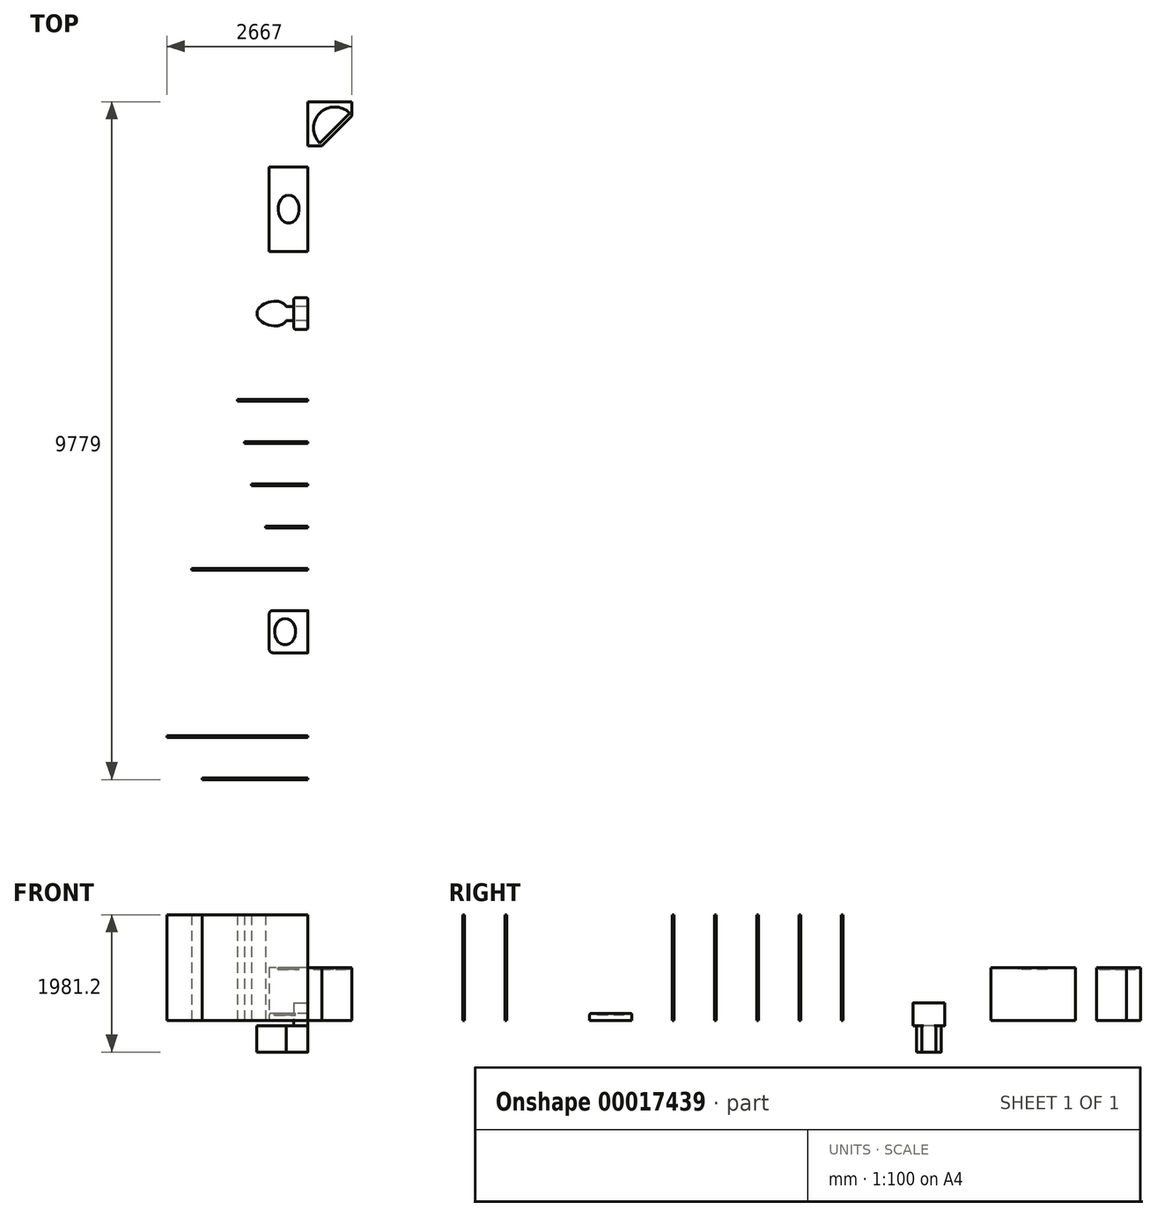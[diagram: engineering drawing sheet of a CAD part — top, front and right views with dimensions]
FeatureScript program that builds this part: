
annotation { "Feature Type Name" : "Feature", "Feature Type Description" : "" }
export const myFeature = defineFeature(function(context is Context, id is Id, definition is map)
    precondition{}
    {
        {
            var Q0;
            Q0=qCreatedBy(makeId("Top.planeOp"),FACE);
            cPlane(context, id + "F0", {"entities" : qUnion([Q0]), "cplaneType" : CPlaneType.OFFSET, "offset" : 457.2 * mm, "width" : 152.4 * mm, "height" : 152.4 * mm});
        }
        {
            var Q0;
            Q0=qCreatedBy(makeId("Top.planeOp"),FACE);
            var sketch = newSketch(context, id + "F1", { "sketchPlane" : qUnion([Q0])});
            skLineSegment(sketch, "E0", {"start": v(0, 702.51) * mm, "end": v(0, 550.11) * mm});
            skLineSegment(sketch, "E1", {"start": v(-25.4, 727.91) * mm, "end": v(-311.29, 727.91) * mm});
            skLineSegment(sketch, "E2", {"start": v(-25.4, 524.71) * mm, "end": v(-311.29, 524.71) * mm});
            skLineSegment(sketch, "E3", {"start": v(-457.2, 626.31) * mm, "end": v(-736.6, 626.31) * mm, "construction": true});
            skLineSegment(sketch, "E4", {"start": v(-457.2, 804.11) * mm, "end": v(-457.2, 448.51) * mm, "construction": true});
            skEllipticalArc(sketch, "E5", {});
            skArc(sketch, "E6", {"start": v(-457.2, 448.51) * mm, "mid": v(-374.9, 468.7) * mm, "end": v(-311.29, 524.71) * mm});
            skArc(sketch, "E7", {"start": v(-311.29, 727.91) * mm, "mid": v(-374.9, 783.92) * mm, "end": v(-457.2, 804.11) * mm});
            skArc(sketch, "E8", {"start": v(-311.29, 524.71) * mm, "mid": v(-279.4, 626.31) * mm, "end": v(-311.29, 727.91) * mm, "construction": true});
            skLineSegment(sketch, "E9", {"start": v(-736.6, 626.31) * mm, "end": v(0, 626.31) * mm, "construction": true});
            skPoint(sketch, "E10.visualSharp", {"position": v(0, 727.91) * mm});
            skArc(sketch, "E10.filletArc", {"start": v(0, 702.51) * mm, "mid": v(-7.44, 720.47) * mm, "end": v(-25.4, 727.91) * mm});
            skPoint(sketch, "E11.visualSharp", {"position": v(0, 524.71) * mm});
            skArc(sketch, "E11.filletArc", {"start": v(-25.4, 524.71) * mm, "mid": v(-7.44, 532.15) * mm, "end": v(0, 550.11) * mm});
            const initialGuessF1  = {"E5": [-0.4572, 0.6263124527790692, 0, 1, 0.1778, 0.2794, 6.283185307179586, 3.141592653589793]};
            skSetInitialGuess(sketch, initialGuessF1);
            skSolve(sketch);
        }
        {
            var Q0;
            Q0 = qSketchRegion(id + "F1", true);
            extrude(context, id + "F2", {"entities" : qUnion([Q0]), "depth" : 381 * mm});
        }
        {
            var Q0;
            Q0=makeQuery(id+"F2.opExtrude","CAP_FACE",FACE,{"disambiguationData":[OSD([sQuery(id+"F1.wireOp",EDGE,"E0"),sQuery(id+"F1.wireOp",EDGE,"E1"),sQuery(id+"F1.wireOp",EDGE,"E2"),sQuery(id+"F1.wireOp",EDGE,"E5"),sQuery(id+"F1.wireOp",EDGE,"E6"),sQuery(id+"F1.wireOp",EDGE,"E7"),sQuery(id+"F1.wireOp",EDGE,"E10.filletArc"),sQuery(id+"F1.wireOp",EDGE,"E11.filletArc")])],"isStart":false});
            var sketch = newSketch(context, id + "F3", { "sketchPlane" : qUnion([Q0])});
            skLineSegment(sketch, "E12.bottom", {"start": v(-177.8, 854.91) * mm, "end": v(-25.4, 854.91) * mm});
            skLineSegment(sketch, "E12.top", {"start": v(-177.8, 397.71) * mm, "end": v(-25.4, 397.71) * mm});
            skLineSegment(sketch, "E12.left", {"start": v(-203.2, 829.51) * mm, "end": v(-203.2, 423.11) * mm});
            skLineSegment(sketch, "E12.right", {"start": v(0, 829.51) * mm, "end": v(0, 423.11) * mm});
            skPoint(sketch, "E13.visualSharp", {"position": v(-203.2, 854.91) * mm});
            skArc(sketch, "E13.filletArc", {"start": v(-177.8, 854.91) * mm, "mid": v(-195.76, 847.47) * mm, "end": v(-203.2, 829.51) * mm});
            skPoint(sketch, "E14.visualSharp", {"position": v(0, 854.91) * mm});
            skArc(sketch, "E14.filletArc", {"start": v(0, 829.51) * mm, "mid": v(-7.44, 847.47) * mm, "end": v(-25.4, 854.91) * mm});
            skPoint(sketch, "E15.visualSharp", {"position": v(0, 397.71) * mm});
            skArc(sketch, "E15.filletArc", {"start": v(-25.4, 397.71) * mm, "mid": v(-7.44, 405.15) * mm, "end": v(0, 423.11) * mm});
            skPoint(sketch, "E16.visualSharp", {"position": v(-203.2, 397.71) * mm});
            skArc(sketch, "E16.filletArc", {"start": v(-203.2, 423.11) * mm, "mid": v(-195.76, 405.15) * mm, "end": v(-177.8, 397.71) * mm});
            skSolve(sketch);
        }
        {
            var Q0;
            Q0 = qSketchRegion(id + "F3", true);
            extrude(context, id + "F4", {"entities" : qUnion([Q0]), "operationType" : NewBodyOperationType.ADD, "depth" : 330.2 * mm});
        }
        {
            var Q0;
            Q0=qCreatedBy(id+"F0.planeOp",FACE);
            var sketch = newSketch(context, id + "F5", { "sketchPlane" : qUnion([Q0])});
            skLineSegment(sketch, "E17.bottom", {"start": v(0, 1524) * mm, "end": v(-558.8, 1524) * mm});
            skLineSegment(sketch, "E17.top", {"start": v(0, 2743.2) * mm, "end": v(-558.8, 2743.2) * mm});
            skLineSegment(sketch, "E17.left", {"start": v(0, 1524) * mm, "end": v(0, 2743.2) * mm});
            skLineSegment(sketch, "E17.right", {"start": v(-558.8, 1524) * mm, "end": v(-558.8, 2743.2) * mm});
            skSolve(sketch);
        }
        {
            var Q0;
            Q0 = qSketchRegion(id + "F5", true);
            extrude(context, id + "F6", {"entities" : qUnion([Q0]), "depth" : 762 * mm});
        }
        {
            var Q0;
            Q0=makeQuery(id+"F6.opExtrude","CAP_FACE",FACE,{"disambiguationData":[OSD([sQuery(id+"F5.wireOp",EDGE,"E17.bottom"),sQuery(id+"F5.wireOp",EDGE,"E17.top"),sQuery(id+"F5.wireOp",EDGE,"E17.left"),sQuery(id+"F5.wireOp",EDGE,"E17.right")])],"isStart":false});
            var sketch = newSketch(context, id + "F7", { "sketchPlane" : qUnion([Q0])});
            skLineSegment(sketch, "E18", {"start": v(0, 2133.6) * mm, "end": v(-558.8, 2133.6) * mm, "construction": true});
            skLineSegment(sketch, "E19", {"start": v(-279.4, 2743.2) * mm, "end": v(-279.4, 1524) * mm, "construction": true});
            skEllipse(sketch, "E20", {"center": v(-279.4, 2133.6) * mm, "majorRadius": 203.15 * mm, "minorRadius": 152.4 * mm, "majorAxis": v(0, 1)});
            skSolve(sketch);
        }
        {
            var Q0;
            Q0 = qSketchRegion(id + "F7", true);
            extrude(context, id + "F8", {"entities" : qUnion([Q0]), "operationType" : NewBodyOperationType.REMOVE, "oppositeDirection" : true, "depth" : 30.48 * mm});
        }
        {
            var Q0;
            Q0=qCreatedBy(id+"F0.planeOp",FACE);
            var sketch = newSketch(context, id + "F9", { "sketchPlane" : qUnion([Q0])});
            skLineSegment(sketch, "E21", {"start": v(0, 3048) * mm, "end": v(203.2, 3048) * mm});
            skLineSegment(sketch, "E22", {"start": v(203.2, 3048) * mm, "end": v(635, 3479.8) * mm});
            skLineSegment(sketch, "E23", {"start": v(635, 3479.8) * mm, "end": v(635, 3683) * mm});
            skLineSegment(sketch, "E24", {"start": v(635, 3683) * mm, "end": v(0, 3683) * mm});
            skLineSegment(sketch, "E25", {"start": v(0, 3683) * mm, "end": v(0, 3048) * mm});
            skSolve(sketch);
        }
        {
            var Q0;
            Q0 = qSketchRegion(id + "F9", true);
            extrude(context, id + "F10", {"entities" : qUnion([Q0]), "depth" : 762 * mm});
        }
        {
            var Q0;
            Q0=makeQuery(id+"F10.opExtrude","CAP_FACE",FACE,{"disambiguationData":[OSD([sQuery(id+"F9.wireOp",EDGE,"E21"),sQuery(id+"F9.wireOp",EDGE,"E22"),sQuery(id+"F9.wireOp",EDGE,"E23"),sQuery(id+"F9.wireOp",EDGE,"E24"),sQuery(id+"F9.wireOp",EDGE,"E25")])],"isStart":false});
            var sketch = newSketch(context, id + "F11", { "sketchPlane" : qUnion([Q0])});
            skLineSegment(sketch, "E26", {"start": v(0, 3683) * mm, "end": v(419.1, 3263.9) * mm, "construction": true});
            skLineSegment(sketch, "E27.0", {"start": v(169.6, 3086.25) * mm, "end": v(600.66, 3517.3) * mm});
            skArc(sketch, "E28", {"start": v(600.66, 3517.3) * mm, "mid": v(169.6, 3517.3) * mm, "end": v(169.6, 3086.25) * mm});
            skSolve(sketch);
        }
        {
            var Q0;
            Q0 = qSketchRegion(id + "F11", true);
            extrude(context, id + "F12", {"entities" : qUnion([Q0]), "operationType" : NewBodyOperationType.REMOVE, "oppositeDirection" : true, "depth" : 30.48 * mm});
        }
        {
            var Q0;
            Q0=qCreatedBy(id+"F0.planeOp",FACE);
            var sketch = newSketch(context, id + "F13", { "sketchPlane" : qUnion([Q0])});
            skLineSegment(sketch, "E29.bottom", {"start": v(0, -5486.4) * mm, "end": v(-2032, -5486.4) * mm});
            skLineSegment(sketch, "E29.top", {"start": v(0, -5461) * mm, "end": v(-2032, -5461) * mm});
            skLineSegment(sketch, "E29.left", {"start": v(0, -5461) * mm, "end": v(0, -5486.4) * mm});
            skLineSegment(sketch, "E29.right", {"start": v(-2032, -5461) * mm, "end": v(-2032, -5486.4) * mm});
            skSolve(sketch);
        }
        {
            var Q0;
            Q0 = qSketchRegion(id + "F13", true);
            extrude(context, id + "F14", {"entities" : qUnion([Q0]), "depth" : 1524 * mm});
        }
        {
            var Q0;
            Q0=qCreatedBy(id+"F0.planeOp",FACE);
            var sketch = newSketch(context, id + "F15", { "sketchPlane" : qUnion([Q0])});
            skLineSegment(sketch, "E30.bottom", {"start": v(0, -6096) * mm, "end": v(-1524, -6096) * mm});
            skLineSegment(sketch, "E30.top", {"start": v(0, -6070.6) * mm, "end": v(-1524, -6070.6) * mm});
            skLineSegment(sketch, "E30.left", {"start": v(0, -6070.6) * mm, "end": v(0, -6096) * mm});
            skLineSegment(sketch, "E30.right", {"start": v(-1524, -6070.6) * mm, "end": v(-1524, -6096) * mm});
            skSolve(sketch);
        }
        {
            var Q0;
            Q0 = qSketchRegion(id + "F15", true);
            extrude(context, id + "F16", {"entities" : qUnion([Q0]), "depth" : 1524 * mm});
        }
        {
            var Q0;
            Q0=qCreatedBy(id+"F0.planeOp",FACE);
            var sketch = newSketch(context, id + "F17", { "sketchPlane" : qUnion([Q0])});
            skLineSegment(sketch, "E31.bottom", {"start": v(0, -609.6) * mm, "end": v(-1016, -609.6) * mm});
            skLineSegment(sketch, "E31.top", {"start": v(0, -635) * mm, "end": v(-1016, -635) * mm});
            skLineSegment(sketch, "E31.left", {"start": v(0, -609.6) * mm, "end": v(0, -635) * mm});
            skLineSegment(sketch, "E31.right", {"start": v(-1016, -609.6) * mm, "end": v(-1016, -635) * mm});
            skSolve(sketch);
        }
        {
            var Q0;
            Q0 = qSketchRegion(id + "F17", true);
            extrude(context, id + "F18", {"entities" : qUnion([Q0]), "depth" : 1524 * mm});
        }
        {
            var Q0;
            Q0=qCreatedBy(id+"F0.planeOp",FACE);
            var sketch = newSketch(context, id + "F19", { "sketchPlane" : qUnion([Q0])});
            skLineSegment(sketch, "E32.bottom", {"start": v(0, -1219.2) * mm, "end": v(-914.4, -1219.2) * mm});
            skLineSegment(sketch, "E32.top", {"start": v(0, -1244.6) * mm, "end": v(-914.4, -1244.6) * mm});
            skLineSegment(sketch, "E32.left", {"start": v(0, -1219.2) * mm, "end": v(0, -1244.6) * mm});
            skLineSegment(sketch, "E32.right", {"start": v(-914.4, -1219.2) * mm, "end": v(-914.4, -1244.6) * mm});
            skSolve(sketch);
        }
        {
            var Q0;
            Q0 = qSketchRegion(id + "F19", true);
            extrude(context, id + "F20", {"entities" : qUnion([Q0]), "depth" : 1524 * mm});
        }
        {
            var Q0;
            Q0=qCreatedBy(id+"F0.planeOp",FACE);
            var sketch = newSketch(context, id + "F21", { "sketchPlane" : qUnion([Q0])});
            skLineSegment(sketch, "E33.bottom", {"start": v(0, -1828.8) * mm, "end": v(-812.8, -1828.8) * mm});
            skLineSegment(sketch, "E33.top", {"start": v(0, -1854.2) * mm, "end": v(-812.8, -1854.2) * mm});
            skLineSegment(sketch, "E33.left", {"start": v(0, -1828.8) * mm, "end": v(0, -1854.2) * mm});
            skLineSegment(sketch, "E33.right", {"start": v(-812.8, -1828.8) * mm, "end": v(-812.8, -1854.2) * mm});
            skSolve(sketch);
        }
        {
            var Q0;
            Q0 = qSketchRegion(id + "F21", true);
            extrude(context, id + "F22", {"entities" : qUnion([Q0]), "depth" : 1524 * mm});
        }
        {
            var Q0;
            Q0=qCreatedBy(id+"F0.planeOp",FACE);
            var sketch = newSketch(context, id + "F23", { "sketchPlane" : qUnion([Q0])});
            skLineSegment(sketch, "E34.bottom", {"start": v(0, -2438.4) * mm, "end": v(-609.6, -2438.4) * mm});
            skLineSegment(sketch, "E34.top", {"start": v(0, -2463.8) * mm, "end": v(-609.6, -2463.8) * mm});
            skLineSegment(sketch, "E34.left", {"start": v(0, -2438.4) * mm, "end": v(0, -2463.8) * mm});
            skLineSegment(sketch, "E34.right", {"start": v(-609.6, -2438.4) * mm, "end": v(-609.6, -2463.8) * mm});
            skSolve(sketch);
        }
        {
            var Q0;
            Q0 = qSketchRegion(id + "F23", true);
            extrude(context, id + "F24", {"entities" : qUnion([Q0]), "depth" : 1524 * mm});
        }
        {
            var Q0;
            Q0=qCreatedBy(id+"F0.planeOp",FACE);
            var sketch = newSketch(context, id + "F25", { "sketchPlane" : qUnion([Q0])});
            skLineSegment(sketch, "E35.bottom", {"start": v(0, -3048) * mm, "end": v(-1676.4, -3048) * mm});
            skLineSegment(sketch, "E35.top", {"start": v(0, -3073.39) * mm, "end": v(-1676.4, -3073.39) * mm});
            skLineSegment(sketch, "E35.left", {"start": v(0, -3048) * mm, "end": v(0, -3073.39) * mm});
            skLineSegment(sketch, "E35.right", {"start": v(-1676.4, -3048) * mm, "end": v(-1676.4, -3073.39) * mm});
            skSolve(sketch);
        }
        {
            var Q0;
            Q0 = qSketchRegion(id + "F25", true);
            extrude(context, id + "F26", {"entities" : qUnion([Q0]), "depth" : 1524 * mm});
        }
        {
            var Q0;
            Q0=qCreatedBy(id+"F0.planeOp",FACE);
            var sketch = newSketch(context, id + "F27", { "sketchPlane" : qUnion([Q0])});
            skLineSegment(sketch, "E36.bottom", {"start": v(0, -3657.6) * mm, "end": v(-508, -3657.6) * mm});
            skLineSegment(sketch, "E36.top", {"start": v(0, -4267.2) * mm, "end": v(-508, -4267.2) * mm});
            skLineSegment(sketch, "E36.left", {"start": v(0, -3657.6) * mm, "end": v(0, -4267.2) * mm});
            skLineSegment(sketch, "E36.right", {"start": v(-558.8, -3708.4) * mm, "end": v(-558.8, -4216.4) * mm});
            skPoint(sketch, "E37.visualSharp", {"position": v(-558.8, -3657.6) * mm});
            skArc(sketch, "E37.filletArc", {"start": v(-508, -3657.6) * mm, "mid": v(-543.92, -3672.48) * mm, "end": v(-558.8, -3708.4) * mm});
            skPoint(sketch, "E38.visualSharp", {"position": v(-558.8, -4267.2) * mm});
            skArc(sketch, "E38.filletArc", {"start": v(-558.8, -4216.4) * mm, "mid": v(-543.92, -4252.32) * mm, "end": v(-508, -4267.2) * mm});
            skSolve(sketch);
        }
        {
            var Q0;
            Q0 = qSketchRegion(id + "F27", true);
            extrude(context, id + "F28", {"entities" : qUnion([Q0]), "depth" : 101.6 * mm});
        }
        {
            var Q0;
            Q0=makeQuery(id+"F28.opExtrude","CAP_FACE",FACE,{"disambiguationData":[OSD([sQuery(id+"F27.wireOp",EDGE,"E36.bottom"),sQuery(id+"F27.wireOp",EDGE,"E36.top"),sQuery(id+"F27.wireOp",EDGE,"E36.left"),sQuery(id+"F27.wireOp",EDGE,"E36.right"),sQuery(id+"F27.wireOp",EDGE,"E37.filletArc"),sQuery(id+"F27.wireOp",EDGE,"E38.filletArc")])],"isStart":false});
            var sketch = newSketch(context, id + "F29", { "sketchPlane" : qUnion([Q0])});
            skLineSegment(sketch, "E39", {"start": v(-558.8, -3962.4) * mm, "end": v(0, -3962.4) * mm, "construction": true});
            skEllipse(sketch, "E40", {"center": v(-330.2, -3962.4) * mm, "majorRadius": 190.5 * mm, "minorRadius": 152.4 * mm, "majorAxis": v(0, 1)});
            skSolve(sketch);
        }
        {
            var Q0;
            Q0 = qSketchRegion(id + "F29", true);
            extrude(context, id + "F30", {"entities" : qUnion([Q0]), "operationType" : NewBodyOperationType.REMOVE, "oppositeDirection" : true, "depth" : 30.48 * mm});
        }
        {
            var Q0;
            Q0=makeQuery(id+"F28.opExtrude","CAP_EDGE",EDGE,{"disambiguationData":[OSD([sQuery(id+"F27.wireOp",EDGE,"E36.right")])],"isStart":false});
            fillet(context, id + "F31", {"entities" : qUnion([Q0]), "radius" : 25.4 * mm, "tangentPropagation" : true, "allowEdgeOverflow" : false});
        }
    });
